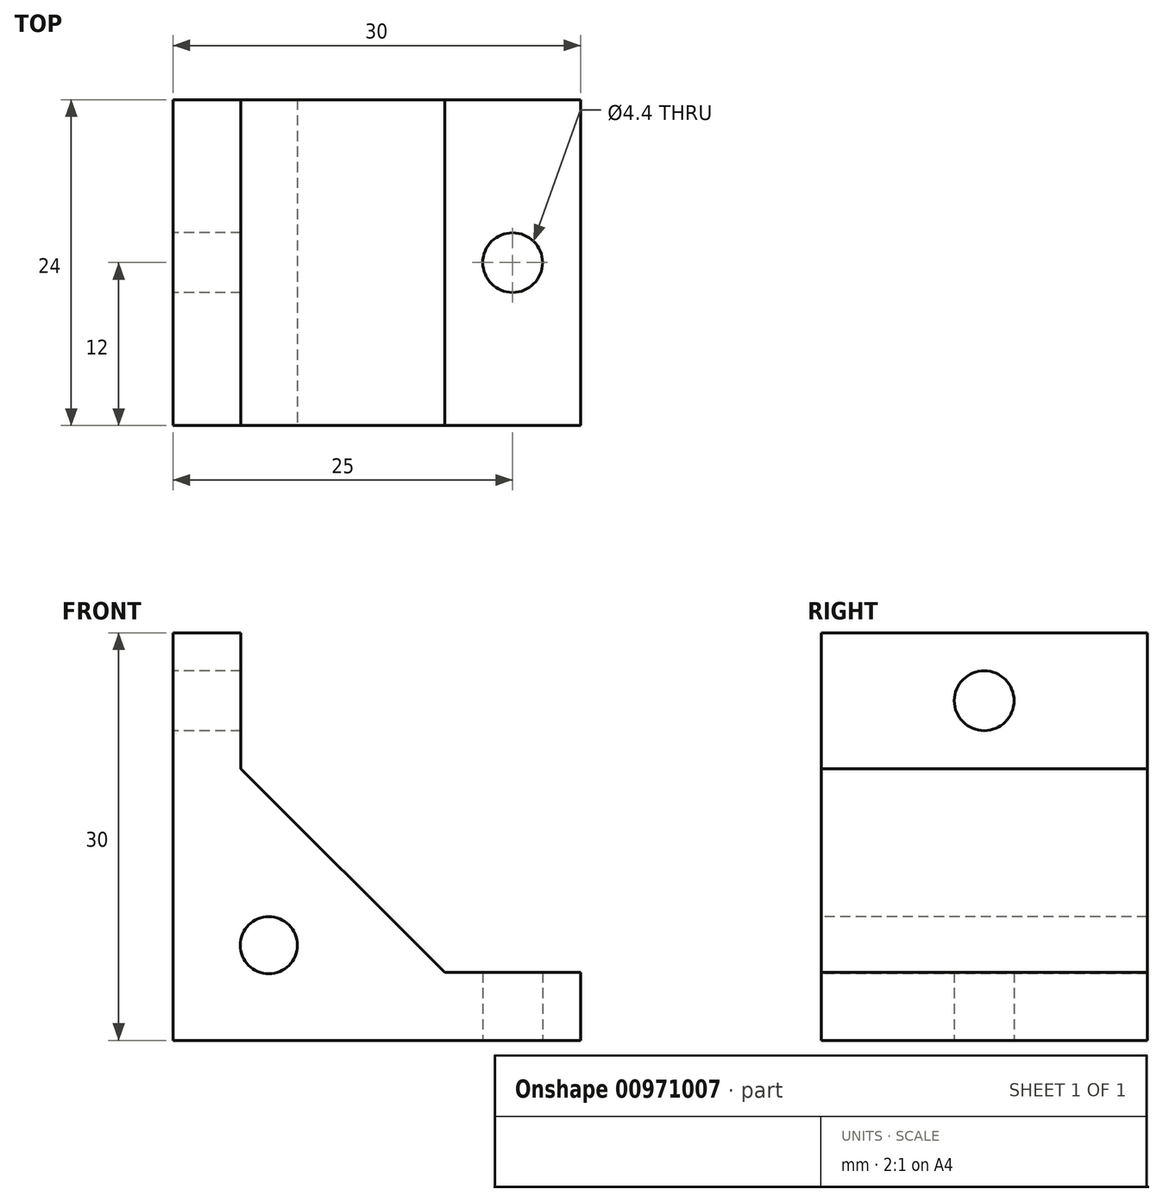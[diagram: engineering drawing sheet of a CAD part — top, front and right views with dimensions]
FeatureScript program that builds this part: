
annotation { "Feature Type Name" : "Feature", "Feature Type Description" : "" }
export const myFeature = defineFeature(function(context is Context, id is Id, definition is map)
    precondition{}
    {
        {
            var Q0;
            Q0=qCreatedBy(makeId("Top.planeOp"),FACE);
            var sketch = newSketch(context, id + "F0", { "sketchPlane" : qUnion([Q0])});
            skLineSegment(sketch, "E0.bottom", {"start": v(0, 0) * mm, "end": v(30, 0) * mm});
            skLineSegment(sketch, "E0.top", {"start": v(0, 24) * mm, "end": v(30, 24) * mm});
            skLineSegment(sketch, "E0.left", {"start": v(0, 0) * mm, "end": v(0, 24) * mm});
            skLineSegment(sketch, "E0.right", {"start": v(30, 0) * mm, "end": v(30, 24) * mm});
            skLineSegment(sketch, "E1.bottom", {"start": v(30, 16) * mm, "end": v(0, 16) * mm});
            skLineSegment(sketch, "E1.top", {"start": v(30, 8) * mm, "end": v(0, 8) * mm});
            skLineSegment(sketch, "E1.left", {"start": v(30, 16) * mm, "end": v(30, 8) * mm});
            skLineSegment(sketch, "E1.right", {"start": v(0, 16) * mm, "end": v(0, 8) * mm});
            skPoint(sketch, "E1.middle", {"position": v(15, 12) * mm});
            skPoint(sketch, "E1.middle.positionSnap0", {"position": v(15, 0) * mm});
            skPoint(sketch, "E1.middle.positionSnap1", {"position": v(0, 12) * mm});
            skPoint(sketch, "E1.centerSnap0", {"position": v(15, 0) * mm});
            skPoint(sketch, "E1.centerSnap1", {"position": v(0, 12) * mm});
            skCircle(sketch, "E2", {"center": v(25, 12) * mm, "radius": 2.2 * mm});
            skSolve(sketch);
        }
        {
            var Q0;
            Q0=qCreatedBy(makeId("Right.planeOp"),FACE);
            var sketch = newSketch(context, id + "F1", { "sketchPlane" : qUnion([Q0])});
            skLineSegment(sketch, "E3.bottom", {"start": v(0, 0) * mm, "end": v(24, 0) * mm});
            skLineSegment(sketch, "E3.top", {"start": v(0, 30) * mm, "end": v(24, 30) * mm});
            skLineSegment(sketch, "E3.left", {"start": v(0, 0) * mm, "end": v(0, 30) * mm});
            skLineSegment(sketch, "E3.right", {"start": v(24, 0) * mm, "end": v(24, 30) * mm});
            skLineSegment(sketch, "E4.bottom", {"start": v(8, 30) * mm, "end": v(16, 30) * mm});
            skLineSegment(sketch, "E4.top", {"start": v(8, 0) * mm, "end": v(16, 0) * mm});
            skLineSegment(sketch, "E4.left", {"start": v(8, 30) * mm, "end": v(8, 0) * mm});
            skLineSegment(sketch, "E4.right", {"start": v(16, 30) * mm, "end": v(16, 0) * mm});
            skCircle(sketch, "E5", {"center": v(12, 25) * mm, "radius": 2.2 * mm});
            skSolve(sketch);
        }
        {
            var Q0;
            {var subQ2=sQuery(id+"F1.wireOp",EDGE,"E3.right");Q0=makeQuery(id+"F1.imprint","IMPRINT",FACE,{"disambiguationData":[TD([[makeQuery(id+"F1.imprint","IMPRINT",EDGE,{"derivedFrom":subQ2}),1.0]])]});}
            var Q1;
            {var subQ1=sQuery(id+"F1.wireOp",EDGE,"E4.left");Q1=makeQuery(id+"F1.imprint","IMPRINT",FACE,{"disambiguationData":[TD([[makeQuery(id+"F1.imprint","IMPRINT",EDGE,{"derivedFrom":subQ1}),1.0]])]});}
            var Q2;
            {var subQ0=sQuery(id+"F1.wireOp",EDGE,"E3.left");Q2=makeQuery(id+"F1.imprint","IMPRINT",FACE,{"disambiguationData":[TD([[makeQuery(id+"F1.imprint","IMPRINT",EDGE,{"derivedFrom":subQ0}),-1.0]])]});}
            extrude(context, id + "F2", {"entities" : qUnion([Q0, Q1, Q2]), "depth" : 5 * mm, "offsetDistance" : 25 * mm});
        }
        {
            var Q0;
            {var subQ0=sQuery(id+"F0.wireOp",EDGE,"E0.top");Q0=makeQuery(id+"F0.imprint","IMPRINT",FACE,{"disambiguationData":[TD([[makeQuery(id+"F0.imprint","IMPRINT",EDGE,{"derivedFrom":subQ0}),-1.0]])]});}
            var Q1;
            {var subQ1=sQuery(id+"F0.wireOp",EDGE,"E1.bottom");Q1=makeQuery(id+"F0.imprint","IMPRINT",FACE,{"disambiguationData":[TD([[makeQuery(id+"F0.imprint","IMPRINT",EDGE,{"derivedFrom":subQ1}),1.0]])]});}
            var Q2;
            {var subQ0=sQuery(id+"F0.wireOp",EDGE,"E0.bottom");Q2=makeQuery(id+"F0.imprint","IMPRINT",FACE,{"disambiguationData":[TD([[makeQuery(id+"F0.imprint","IMPRINT",EDGE,{"derivedFrom":subQ0}),1.0]])]});}
            extrude(context, id + "F3", {"entities" : qUnion([Q0, Q1, Q2]), "operationType" : NewBodyOperationType.ADD, "depth" : 5 * mm, "offsetDistance" : 25 * mm});
        }
        {
            var Q0;
            Q0=qCreatedBy(makeId("Front.planeOp"),FACE);
            var sketch = newSketch(context, id + "F4", { "sketchPlane" : qUnion([Q0])});
            skLineSegment(sketch, "E6", {"start": v(20, 0) * mm, "end": v(0, 20) * mm});
            skLineSegment(sketch, "E7", {"start": v(2.66, 17.34) * mm, "end": v(17.64, 2.36) * mm});
            skLineSegment(sketch, "E8", {"start": v(2.66, 17.34) * mm, "end": v(2.66, 2.36) * mm});
            skLineSegment(sketch, "E9", {"start": v(2.66, 2.36) * mm, "end": v(17.64, 2.36) * mm});
            skCircle(sketch, "E10", {"center": v(7.04, 7) * mm, "radius": 5 * mm});
            skCircle(sketch, "E11", {"center": v(7.04, 7) * mm, "radius": 2.1 * mm});
            skSolve(sketch);
        }
        {
            var Q0;
            Q0=makeQuery(id+"F3.boolean.opBoolean","INTERSECT",EDGE,{"derivedFrom":[makeQuery(id+"F2.opExtrude","CAP_FACE",FACE,{"disambiguationData":[OSD([sQuery(id+"F1.wireOp",EDGE,"E3.bottom"),sQuery(id+"F1.wireOp",EDGE,"E3.top"),sQuery(id+"F1.wireOp",EDGE,"E3.left"),sQuery(id+"F1.wireOp",EDGE,"E3.right"),sQuery(id+"F1.wireOp",EDGE,"E5")])],"isStart":false}),makeQuery(id+"F3.opExtrude","CAP_FACE",FACE,{"disambiguationData":[OSD([sQuery(id+"F0.wireOp",EDGE,"E0.bottom"),sQuery(id+"F0.wireOp",EDGE,"E0.top"),sQuery(id+"F0.wireOp",EDGE,"E0.left"),sQuery(id+"F0.wireOp",EDGE,"E0.right"),sQuery(id+"F0.wireOp",EDGE,"E2")])],"isStart":false})]});
            chamfer(context, id + "F5", {"entities" : qUnion([Q0]), "width" : 15 * mm, "tangentPropagation" : true});
        }
        {
            var Q0;
            Q0=makeQuery(id+"F4.imprint","IMPRINT",FACE,{"disambiguationData":[TD([[makeQuery(id+"F4.imprint","IMPRINT",EDGE,{"derivedFrom":sQuery(id+"F4.wireOp",EDGE,"E7")}),-1.0]])]});
            var Q1;
            Q1=makeQuery(id+"F4.imprint","IMPRINT",FACE,{"disambiguationData":[TD([[makeQuery(id+"F4.imprint","IMPRINT",EDGE,{"derivedFrom":sQuery(id+"F4.wireOp",EDGE,"E11")}),1.0]])]});
            extrude(context, id + "F6", {"entities" : qUnion([Q0, Q1]), "operationType" : NewBodyOperationType.REMOVE, "oppositeDirection" : true, "depth" : 30 * mm, "offsetDistance" : 25 * mm});
        }
    });
